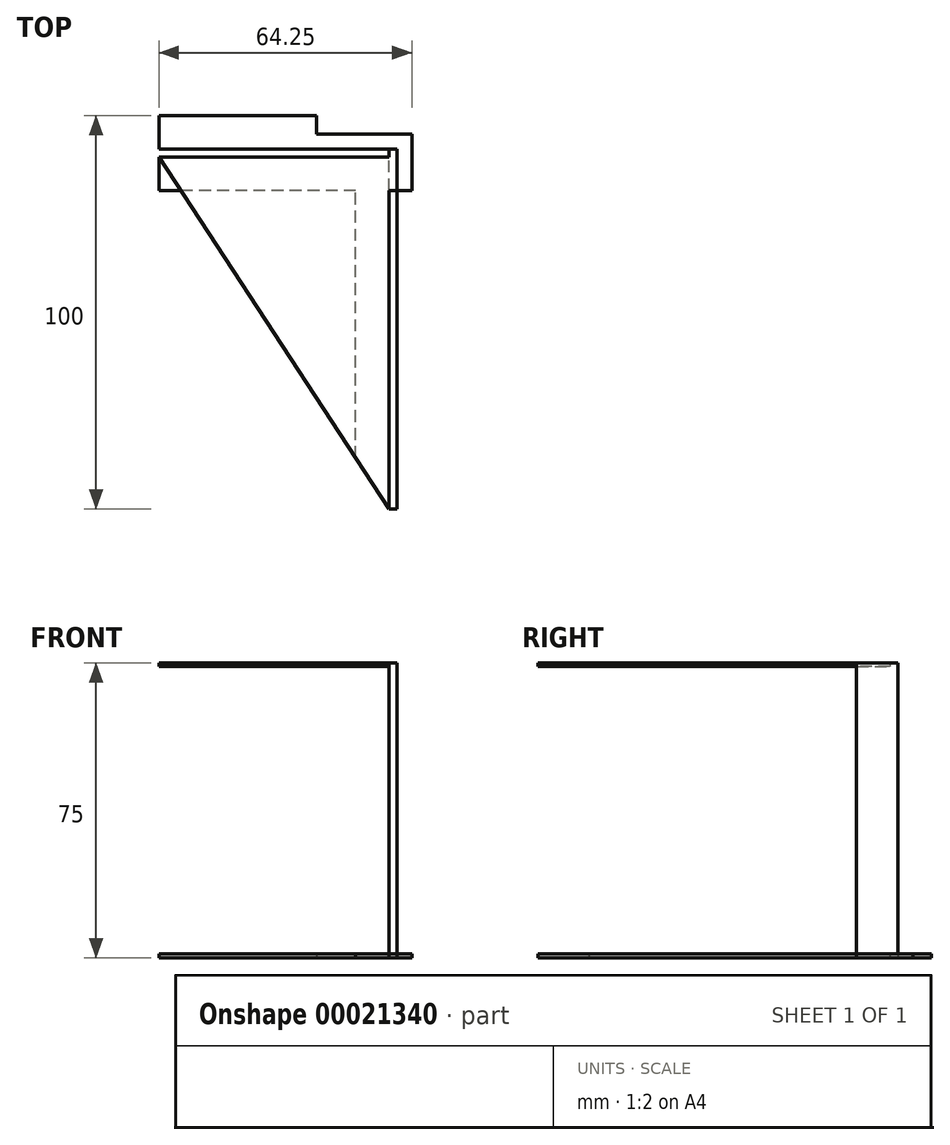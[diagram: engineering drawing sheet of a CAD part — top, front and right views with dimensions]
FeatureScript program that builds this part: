
annotation { "Feature Type Name" : "Feature", "Feature Type Description" : "" }
export const myFeature = defineFeature(function(context is Context, id is Id, definition is map)
    precondition{}
    {
        {
            var Q0;
            Q0=qCreatedBy(makeId("Top.planeOp"),FACE);
            var sketch = newSketch(context, id + "F0", { "sketchPlane" : qUnion([Q0])});
            skLineSegment(sketch, "E0.bottom", {"start": v(10.77, -39.96) * mm, "end": v(29.77, -39.96) * mm});
            skLineSegment(sketch, "E0.top", {"start": v(10.77, 60.04) * mm, "end": v(29.77, 60.04) * mm});
            skLineSegment(sketch, "E0.left", {"start": v(10.77, -39.96) * mm, "end": v(10.77, 60.04) * mm});
            skLineSegment(sketch, "E0.right", {"start": v(29.77, -39.96) * mm, "end": v(29.77, 60.04) * mm});
            skLineSegment(sketch, "E1.bottom", {"start": v(10.77, 60.04) * mm, "end": v(-39.23, 60.04) * mm});
            skLineSegment(sketch, "E1.top", {"start": v(10.77, 41.04) * mm, "end": v(-39.23, 41.04) * mm});
            skLineSegment(sketch, "E1.left", {"start": v(10.77, 60.04) * mm, "end": v(10.77, 41.04) * mm});
            skLineSegment(sketch, "E1.right", {"start": v(-39.23, 60.04) * mm, "end": v(-39.23, 41.04) * mm});
            skPoint(sketch, "E2", {"position": v(20.27, -39.96) * mm});
            skLineSegment(sketch, "E3", {"start": v(20.27, -39.96) * mm, "end": v(10.77, -39.96) * mm});
            skLineSegment(sketch, "E4.bottom", {"start": v(15.52, -39.96) * mm, "end": v(25.02, -39.96) * mm});
            skLineSegment(sketch, "E4.top", {"start": v(15.52, 60.04) * mm, "end": v(25.02, 60.04) * mm});
            skLineSegment(sketch, "E5", {"start": v(20.27, -39.96) * mm, "end": v(25.02, -39.96) * mm});
            skLineSegment(sketch, "E6", {"start": v(20.27, -39.96) * mm, "end": v(15.52, -39.96) * mm});
            skPoint(sketch, "E7", {"position": v(10.77, 50.54) * mm});
            skLineSegment(sketch, "E8", {"start": v(10.77, 41.04) * mm, "end": v(29.77, 41.04) * mm});
            skLineSegment(sketch, "E9", {"start": v(25.02, 60.04) * mm, "end": v(25.02, 41.04) * mm});
            skLineSegment(sketch, "E10", {"start": v(10.77, 50.54) * mm, "end": v(10.77, 60.04) * mm});
            skPoint(sketch, "E11", {"position": v(10.77, 55.3) * mm});
            skLineSegment(sketch, "E12", {"start": v(10.77, 55.3) * mm, "end": v(25.02, 55.3) * mm});
            skLineSegment(sketch, "E13", {"start": v(25.02, 41.04) * mm, "end": v(25.02, 31.04) * mm});
            skLineSegment(sketch, "E14", {"start": v(10.77, 55.3) * mm, "end": v(0.77, 55.3) * mm});
            skLineSegment(sketch, "E15", {"start": v(0.77, 55.3) * mm, "end": v(0.77, 60.04) * mm});
            skLineSegment(sketch, "E16", {"start": v(25.02, 31.04) * mm, "end": v(29.77, 31.04) * mm});
            skLineSegment(sketch, "E17", {"start": v(20.27, -39.96) * mm, "end": v(20.27, 55.3) * mm, "construction": true});
            skPoint(sketch, "E17.endSnap0", {"position": v(17.9, 55.3) * mm});
            skLineSegment(sketch, "E18.0", {"start": v(21.27, -39.96) * mm, "end": v(21.27, 55.3) * mm});
            skLineSegment(sketch, "E19.MirrorCS", {"start": v(19.27, -39.96) * mm, "end": v(19.27, 55.3) * mm});
            skPoint(sketch, "E20", {"position": v(-39.23, 50.54) * mm});
            skLineSegment(sketch, "E21", {"start": v(-39.23, 50.54) * mm, "end": v(21.27, 50.54) * mm, "construction": true});
            skLineSegment(sketch, "E22.0", {"start": v(-39.23, 49.54) * mm, "end": v(21.27, 49.54) * mm});
            skLineSegment(sketch, "E23.MirrorCS", {"start": v(-39.23, 51.54) * mm, "end": v(21.27, 51.54) * mm});
            skLineSegment(sketch, "E24", {"start": v(-39.23, 49.54) * mm, "end": v(19.27, -39.96) * mm});
            skSolve(sketch);
        }
        {
            var Q0;
            {var subQ0=sQuery(id+"F0.wireOp",EDGE,"E14");Q0=makeQuery(id+"F0.imprint","IMPRINT",FACE,{"disambiguationData":[TD([[makeQuery(id+"F0.imprint","IMPRINT",EDGE,{"derivedFrom":subQ0}),1.0]])]});}
            var Q1;
            {var subQ1=sQuery(id+"F0.wireOp",EDGE,"E1.top");var subQ5=sQuery(id+"F0.wireOp",EDGE,"E1.right");var subQ6=makeQuery(id+"F0.imprint","INTERSECT",VERTEX,{"derivedFrom":[subQ1,subQ5]});Q1=makeQuery(id+"F0.imprint","IMPRINT",FACE,{"disambiguationData":[TD([[makeQuery(id+"F0.imprint","IMPRINT",EDGE,{"disambiguationData":[TD([[subQ6,1.0]])],"derivedFrom":subQ1}),-1.0]])]});}
            var Q2;
            {var subQ0=sQuery(id+"F0.wireOp",EDGE,"E8");var subQ5=sQuery(id+"F0.wireOp",EDGE,"E19.MirrorCS");var subQ7=makeQuery(id+"F0.imprint","INTERSECT",VERTEX,{"derivedFrom":[subQ0,subQ5]});Q2=makeQuery(id+"F0.imprint","IMPRINT",FACE,{"disambiguationData":[TD([[makeQuery(id+"F0.imprint","IMPRINT",EDGE,{"disambiguationData":[TD([[subQ7,1.0]])],"derivedFrom":subQ5}),1.0]])]});}
            var Q3;
            {var subQ1=sQuery(id+"F0.wireOp",EDGE,"E0.bottom");Q3=makeQuery(id+"F0.imprint","IMPRINT",FACE,{"disambiguationData":[TD([[makeQuery(id+"F0.imprint","IMPRINT",EDGE,{"derivedFrom":subQ1}),1.0]])]});}
            var Q4;
            {var subQ0=sQuery(id+"F0.wireOp",EDGE,"E3");Q4=makeQuery(id+"F0.imprint","IMPRINT",FACE,{"disambiguationData":[TD([[makeQuery(id+"F0.imprint","IMPRINT",EDGE,{"derivedFrom":subQ0}),-1.0]])]});}
            var Q5;
            {var subQ0=sQuery(id+"F0.wireOp",EDGE,"E8");var subQ5=sQuery(id+"F0.wireOp",EDGE,"E19.MirrorCS");var subQ6=makeQuery(id+"F0.imprint","INTERSECT",VERTEX,{"derivedFrom":[subQ0,subQ5]});Q5=makeQuery(id+"F0.imprint","IMPRINT",FACE,{"disambiguationData":[TD([[makeQuery(id+"F0.imprint","IMPRINT",EDGE,{"disambiguationData":[TD([[subQ6,-1.0]])],"derivedFrom":subQ5}),1.0]])]});}
            var Q6;
            {var subQ0=sQuery(id+"F0.wireOp",EDGE,"E5");var subQ1=sQuery(id+"F0.wireOp",EDGE,"E6");var subQ2=makeQuery(id+"F0.imprint","INTERSECT",VERTEX,{"derivedFrom":[subQ1,subQ0]});Q6=makeQuery(id+"F0.imprint","IMPRINT",FACE,{"disambiguationData":[TD([[makeQuery(id+"F0.imprint","IMPRINT",EDGE,{"disambiguationData":[TD([[subQ2,-1.0]])],"derivedFrom":subQ0}),1.0]])]});}
            var Q7;
            {var subQ0=sQuery(id+"F0.wireOp",EDGE,"E10");var subQ1=sQuery(id+"F0.wireOp",EDGE,"E1.left");var subQ2=makeQuery(id+"F0.imprint","INTERSECT",VERTEX,{"derivedFrom":[subQ1,subQ0]});Q7=makeQuery(id+"F0.imprint","IMPRINT",FACE,{"disambiguationData":[TD([[makeQuery(id+"F0.imprint","IMPRINT",EDGE,{"disambiguationData":[TD([[subQ2,-1.0]])],"derivedFrom":subQ1}),-1.0]])]});}
            var Q8;
            {var subQ0=sQuery(id+"F0.wireOp",EDGE,"E19.MirrorCS");var subQ1=sQuery(id+"F0.wireOp",EDGE,"E8");var subQ2=makeQuery(id+"F0.imprint","INTERSECT",VERTEX,{"derivedFrom":[subQ1,subQ0]});Q8=makeQuery(id+"F0.imprint","IMPRINT",FACE,{"disambiguationData":[TD([[makeQuery(id+"F0.imprint","IMPRINT",EDGE,{"disambiguationData":[TD([[subQ2,-1.0]])],"derivedFrom":subQ1}),1.0]])]});}
            var Q9;
            {var subQ0=sQuery(id+"F0.wireOp",EDGE,"E12");var subQ1=sQuery(id+"F0.wireOp",EDGE,"E9");var subQ2=makeQuery(id+"F0.imprint","INTERSECT",VERTEX,{"derivedFrom":[subQ1,subQ0]});Q9=makeQuery(id+"F0.imprint","IMPRINT",FACE,{"disambiguationData":[TD([[makeQuery(id+"F0.imprint","IMPRINT",EDGE,{"disambiguationData":[TD([[subQ2,1.0]])],"derivedFrom":subQ0}),-1.0]])]});}
            var Q10;
            {var subQ0=sQuery(id+"F0.wireOp",EDGE,"E12");var subQ5=sQuery(id+"F0.wireOp",EDGE,"E19.MirrorCS");var subQ6=makeQuery(id+"F0.imprint","INTERSECT",VERTEX,{"derivedFrom":[subQ0,subQ5]});Q10=makeQuery(id+"F0.imprint","IMPRINT",FACE,{"disambiguationData":[TD([[makeQuery(id+"F0.imprint","IMPRINT",EDGE,{"disambiguationData":[TD([[subQ6,1.0]])],"derivedFrom":subQ5}),1.0]])]});}
            var Q11;
            {var subQ1=sQuery(id+"F0.wireOp",EDGE,"E1.left");var subQ7=sQuery(id+"F0.wireOp",EDGE,"E10");var subQ8=makeQuery(id+"F0.imprint","INTERSECT",VERTEX,{"derivedFrom":[subQ1,subQ7]});Q11=makeQuery(id+"F0.imprint","IMPRINT",FACE,{"disambiguationData":[TD([[makeQuery(id+"F0.imprint","IMPRINT",EDGE,{"disambiguationData":[TD([[subQ8,-1.0]])],"derivedFrom":subQ1}),1.0]])]});}
            var Q12;
            {var subQ0=sQuery(id+"F0.wireOp",EDGE,"E18.0");var subQ1=sQuery(id+"F0.wireOp",EDGE,"E12");var subQ2=makeQuery(id+"F0.imprint","INTERSECT",VERTEX,{"derivedFrom":[subQ1,subQ0]});Q12=makeQuery(id+"F0.imprint","IMPRINT",FACE,{"disambiguationData":[TD([[makeQuery(id+"F0.imprint","IMPRINT",EDGE,{"disambiguationData":[TD([[subQ2,1.0]])],"derivedFrom":subQ1}),-1.0]])]});}
            var Q13;
            {var subQ0=sQuery(id+"F0.wireOp",EDGE,"E22.0");var subQ1=sQuery(id+"F0.wireOp",EDGE,"E18.0");var subQ2=makeQuery(id+"F0.imprint","INTERSECT",VERTEX,{"derivedFrom":[subQ1,subQ0]});Q13=makeQuery(id+"F0.imprint","IMPRINT",FACE,{"disambiguationData":[TD([[makeQuery(id+"F0.imprint","IMPRINT",EDGE,{"disambiguationData":[TD([[subQ2,-1.0]])],"derivedFrom":subQ1}),1.0]])]});}
            var Q14;
            {var subQ0=sQuery(id+"F0.wireOp",EDGE,"E1.left");var subQ5=sQuery(id+"F0.wireOp",EDGE,"E22.0");var subQ6=makeQuery(id+"F0.imprint","INTERSECT",VERTEX,{"derivedFrom":[subQ0,subQ5]});Q14=makeQuery(id+"F0.imprint","IMPRINT",FACE,{"disambiguationData":[TD([[makeQuery(id+"F0.imprint","IMPRINT",EDGE,{"disambiguationData":[TD([[subQ6,1.0]])],"derivedFrom":subQ5}),-1.0]])]});}
            extrude(context, id + "F1", {"entities" : qUnion([Q0, Q1, Q2, Q3, Q4, Q5, Q6, Q7, Q8, Q9, Q10, Q11, Q12, Q13, Q14]), "depth" : 1 * mm, "offsetDistance" : 25 * mm});
        }
        {
            var Q0;
            {var subQ0=sQuery(id+"F0.wireOp",EDGE,"E5");var subQ1=sQuery(id+"F0.wireOp",EDGE,"E6");var subQ2=makeQuery(id+"F0.imprint","INTERSECT",VERTEX,{"derivedFrom":[subQ1,subQ0]});Q0=makeQuery(id+"F0.imprint","IMPRINT",FACE,{"disambiguationData":[TD([[makeQuery(id+"F0.imprint","IMPRINT",EDGE,{"disambiguationData":[TD([[subQ2,-1.0]])],"derivedFrom":subQ0}),1.0]])]});}
            var Q1;
            {var subQ0=sQuery(id+"F0.wireOp",EDGE,"E19.MirrorCS");var subQ1=sQuery(id+"F0.wireOp",EDGE,"E8");var subQ2=makeQuery(id+"F0.imprint","INTERSECT",VERTEX,{"derivedFrom":[subQ1,subQ0]});Q1=makeQuery(id+"F0.imprint","IMPRINT",FACE,{"disambiguationData":[TD([[makeQuery(id+"F0.imprint","IMPRINT",EDGE,{"disambiguationData":[TD([[subQ2,-1.0]])],"derivedFrom":subQ1}),1.0]])]});}
            var Q2;
            {var subQ0=sQuery(id+"F0.wireOp",EDGE,"E22.0");var subQ1=sQuery(id+"F0.wireOp",EDGE,"E18.0");var subQ2=makeQuery(id+"F0.imprint","INTERSECT",VERTEX,{"derivedFrom":[subQ1,subQ0]});Q2=makeQuery(id+"F0.imprint","IMPRINT",FACE,{"disambiguationData":[TD([[makeQuery(id+"F0.imprint","IMPRINT",EDGE,{"disambiguationData":[TD([[subQ2,-1.0]])],"derivedFrom":subQ1}),1.0]])]});}
            var Q3;
            {var subQ1=sQuery(id+"F0.wireOp",EDGE,"E1.left");var subQ7=sQuery(id+"F0.wireOp",EDGE,"E10");var subQ8=makeQuery(id+"F0.imprint","INTERSECT",VERTEX,{"derivedFrom":[subQ1,subQ7]});Q3=makeQuery(id+"F0.imprint","IMPRINT",FACE,{"disambiguationData":[TD([[makeQuery(id+"F0.imprint","IMPRINT",EDGE,{"disambiguationData":[TD([[subQ8,-1.0]])],"derivedFrom":subQ1}),1.0]])]});}
            var Q4;
            {var subQ0=sQuery(id+"F0.wireOp",EDGE,"E10");var subQ1=sQuery(id+"F0.wireOp",EDGE,"E1.left");var subQ2=makeQuery(id+"F0.imprint","INTERSECT",VERTEX,{"derivedFrom":[subQ1,subQ0]});Q4=makeQuery(id+"F0.imprint","IMPRINT",FACE,{"disambiguationData":[TD([[makeQuery(id+"F0.imprint","IMPRINT",EDGE,{"disambiguationData":[TD([[subQ2,-1.0]])],"derivedFrom":subQ1}),-1.0]])]});}
            extrude(context, id + "F2", {"entities" : qUnion([Q0, Q1, Q2, Q3, Q4]), "operationType" : NewBodyOperationType.ADD, "depth" : 75 * mm, "offsetDistance" : 25 * mm});
        }
        {
            var Q0;
            {var subQ0=sQuery(id+"F0.wireOp",EDGE,"E1.left");var subQ5=sQuery(id+"F0.wireOp",EDGE,"E22.0");var subQ6=makeQuery(id+"F0.imprint","INTERSECT",VERTEX,{"derivedFrom":[subQ0,subQ5]});Q0=makeQuery(id+"F0.imprint","IMPRINT",FACE,{"disambiguationData":[TD([[makeQuery(id+"F0.imprint","IMPRINT",EDGE,{"disambiguationData":[TD([[subQ6,1.0]])],"derivedFrom":subQ5}),-1.0]])]});}
            var Q1;
            {var subQ1=sQuery(id+"F0.wireOp",EDGE,"E0.left");var subQ3=sQuery(id+"F0.wireOp",EDGE,"E24");var subQ4=makeQuery(id+"F0.imprint","INTERSECT",VERTEX,{"derivedFrom":[subQ1,subQ3]});Q1=makeQuery(id+"F0.imprint","IMPRINT",FACE,{"disambiguationData":[TD([[makeQuery(id+"F0.imprint","IMPRINT",EDGE,{"disambiguationData":[TD([[subQ4,1.0]])],"derivedFrom":subQ3}),1.0]])]});}
            var Q2;
            {var subQ0=sQuery(id+"F0.wireOp",EDGE,"E8");var subQ5=sQuery(id+"F0.wireOp",EDGE,"E19.MirrorCS");var subQ6=makeQuery(id+"F0.imprint","INTERSECT",VERTEX,{"derivedFrom":[subQ0,subQ5]});Q2=makeQuery(id+"F0.imprint","IMPRINT",FACE,{"disambiguationData":[TD([[makeQuery(id+"F0.imprint","IMPRINT",EDGE,{"disambiguationData":[TD([[subQ6,-1.0]])],"derivedFrom":subQ5}),1.0]])]});}
            var Q3;
            {var subQ0=sQuery(id+"F0.wireOp",EDGE,"E8");var subQ5=sQuery(id+"F0.wireOp",EDGE,"E19.MirrorCS");var subQ6=makeQuery(id+"F0.imprint","INTERSECT",VERTEX,{"derivedFrom":[subQ0,subQ5]});Q3=makeQuery(id+"F0.imprint","IMPRINT",FACE,{"disambiguationData":[TD([[makeQuery(id+"F0.imprint","IMPRINT",EDGE,{"disambiguationData":[TD([[subQ6,1.0]])],"derivedFrom":subQ5}),1.0]])]});}
            var Q4;
            Q4=makeQuery(id+"F2.opExtrude","CAP_FACE",FACE,{"disambiguationData":[OSD([sQuery(id+"F0.wireOp",EDGE,"E1.right"),sQuery(id+"F0.wireOp",EDGE,"E6"),sQuery(id+"F0.wireOp",EDGE,"E5"),sQuery(id+"F0.wireOp",EDGE,"E18.0"),sQuery(id+"F0.wireOp",EDGE,"E19.MirrorCS"),sQuery(id+"F0.wireOp",EDGE,"E22.0"),sQuery(id+"F0.wireOp",EDGE,"E23.MirrorCS")])],"isStart":false});
            extrude(context, id + "F3", {"entities" : qUnion([Q0, Q1, Q2, Q3]), "operationType" : NewBodyOperationType.ADD, "endBound" : BoundingType.UP_TO_SURFACE, "depth" : 1 * mm, "endBoundEntityFace" : qUnion([Q4]), "offsetDistance" : 25 * mm, "hasSecondDirection" : true, "secondDirectionOppositeDirection" : false, "secondDirectionDepth" : 74 * mm, "hasSecondDirectionOffset" : true, "secondDirectionOffsetDistance" : 25 * mm});
        }
    });
